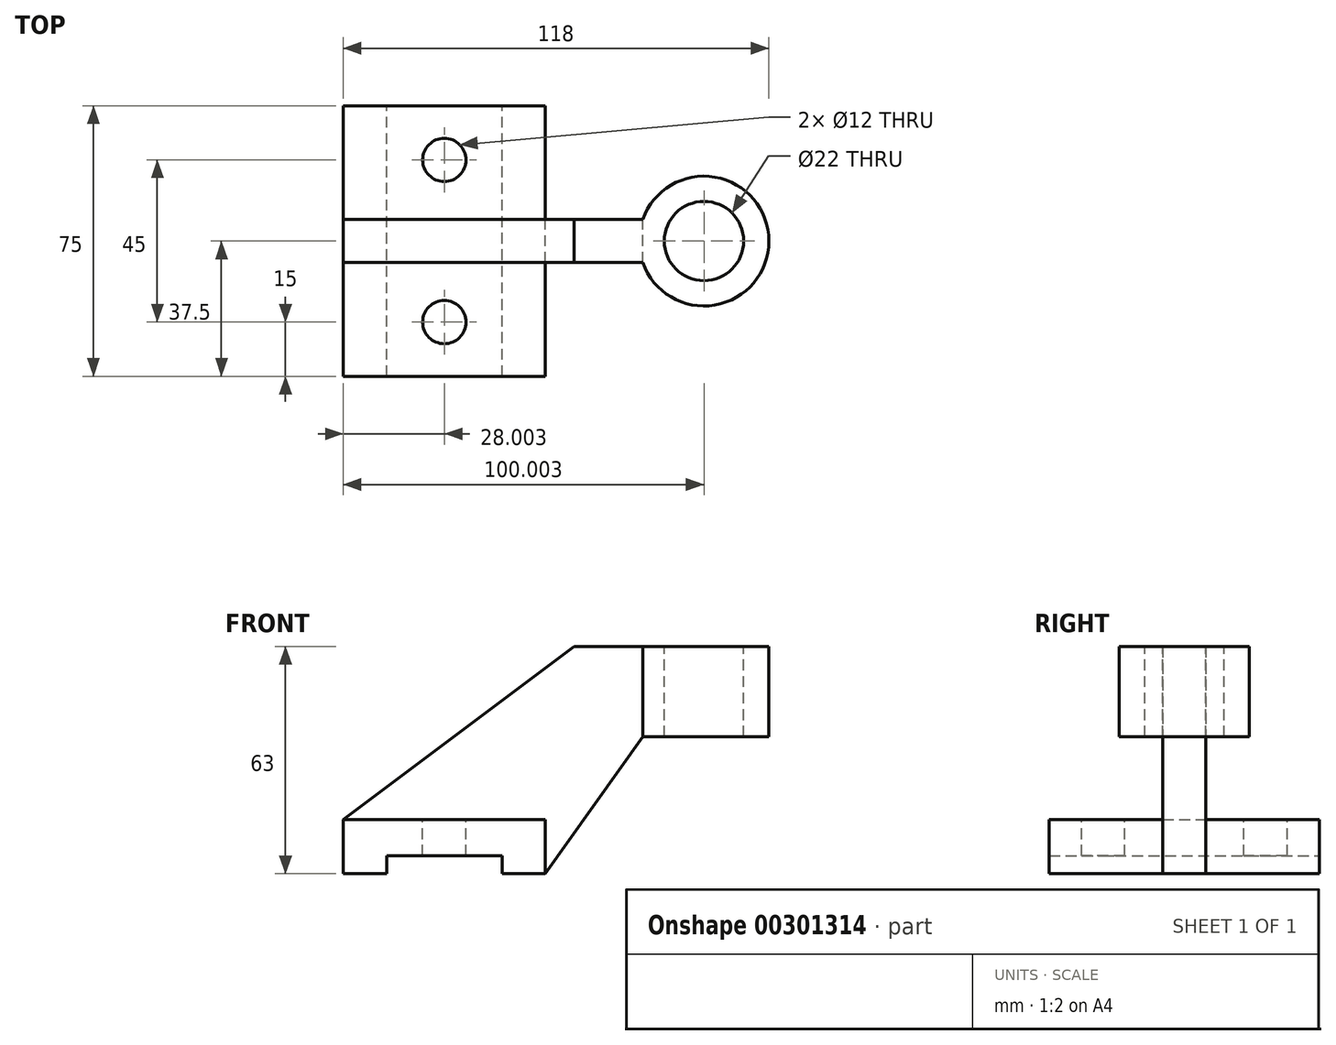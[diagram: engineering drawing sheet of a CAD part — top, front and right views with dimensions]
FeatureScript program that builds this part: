
annotation { "Feature Type Name" : "Feature", "Feature Type Description" : "" }
export const myFeature = defineFeature(function(context is Context, id is Id, definition is map)
    precondition{}
    {
        {
            var Q0;
            Q0=qCreatedBy(makeId("Top.planeOp"),FACE);
            var sketch = newSketch(context, id + "F0", { "sketchPlane" : qUnion([Q0])});
            skCircle(sketch, "E0", {"center": v(33.67, 0) * mm, "radius": 18 * mm});
            skCircle(sketch, "E1", {"center": v(33.67, 0) * mm, "radius": 11 * mm});
            skLineSegment(sketch, "E2", {"start": v(0, 0) * mm, "end": v(20, 0) * mm, "construction": true});
            skLineSegment(sketch, "E3", {"start": v(0, 0) * mm, "end": v(0, 6) * mm, "construction": true});
            skLineSegment(sketch, "E4", {"start": v(0, 6) * mm, "end": v(16.7, 6) * mm, "construction": true});
            skLineSegment(sketch, "E5", {"start": v(33.67, 0) * mm, "end": v(33.67, 22.5) * mm, "construction": true});
            skLineSegment(sketch, "E6", {"start": v(33.67, 22.5) * mm, "end": v(-38.33, 22.5) * mm, "construction": true});
            skLineSegment(sketch, "E7", {"start": v(-38.33, 22.5) * mm, "end": v(-38.33, -22.5) * mm, "construction": true});
            skCircle(sketch, "E8", {"center": v(-38.33, 22.5) * mm, "radius": 6 * mm});
            skCircle(sketch, "E9", {"center": v(-38.33, -22.5) * mm, "radius": 6 * mm});
            skLineSegment(sketch, "E10", {"start": v(16.7, 6) * mm, "end": v(16.7, 0) * mm, "construction": true});
            skPoint(sketch, "E11", {"position": v(16.7, 0) * mm});
            skSolve(sketch);
        }
        {
            var Q0;
            Q0=qCreatedBy(makeId("Front.planeOp"),FACE);
            var sketch = newSketch(context, id + "F1", { "sketchPlane" : qUnion([Q0])});
            skLineSegment(sketch, "E12", {"start": v(-66.33, -63) * mm, "end": v(-54.33, -63) * mm});
            skLineSegment(sketch, "E13", {"start": v(-54.33, -63) * mm, "end": v(-54.33, -58) * mm});
            skLineSegment(sketch, "E14", {"start": v(-54.33, -58) * mm, "end": v(-22.33, -58) * mm});
            skLineSegment(sketch, "E15", {"start": v(-22.33, -58) * mm, "end": v(-22.33, -63) * mm});
            skLineSegment(sketch, "E16", {"start": v(-22.33, -63) * mm, "end": v(-10.33, -63) * mm});
            skLineSegment(sketch, "E17", {"start": v(-10.33, -63) * mm, "end": v(-10.33, -48) * mm});
            skLineSegment(sketch, "E18", {"start": v(-10.33, -48) * mm, "end": v(-66.33, -48) * mm});
            skLineSegment(sketch, "E19", {"start": v(-66.33, -48) * mm, "end": v(-66.33, -63) * mm});
            skLineSegment(sketch, "E20", {"start": v(51.7, 0) * mm, "end": v(51.7, -25) * mm});
            skLineSegment(sketch, "E21", {"start": v(16.7, 0) * mm, "end": v(16.7, -25) * mm});
            skLineSegment(sketch, "E22", {"start": v(16.7, -25) * mm, "end": v(51.7, -25) * mm});
            skLineSegment(sketch, "E23", {"start": v(-10.33, -63) * mm, "end": v(16.7, -25) * mm});
            skLineSegment(sketch, "E24", {"start": v(-66.33, -48) * mm, "end": v(-2.33, 0) * mm});
            skLineSegment(sketch, "E25", {"start": v(-2.33, 0) * mm, "end": v(16.7, 0) * mm});
            skLineSegment(sketch, "E26", {"start": v(16.7, 0) * mm, "end": v(51.7, 0) * mm});
            skSolve(sketch);
        }
        {
            var Q0;
            Q0=makeQuery(id+"F1.imprint","IMPRINT",FACE,{"disambiguationData":[TD([[makeQuery(id+"F1.imprint","IMPRINT",EDGE,{"derivedFrom":sQuery(id+"F1.wireOp",EDGE,"E12")}),1.0]])]});
            extrude(context, id + "F2", {"entities" : qUnion([Q0]), "endBound" : BoundingType.SYMMETRIC, "depth" : 75 * mm});
        }
        {
            var Q0;
            Q0=makeQuery(id+"F1.imprint","IMPRINT",FACE,{"disambiguationData":[TD([[makeQuery(id+"F1.imprint","IMPRINT",EDGE,{"derivedFrom":sQuery(id+"F1.wireOp",EDGE,"E17")}),-1.0]])]});
            extrude(context, id + "F3", {"entities" : qUnion([Q0]), "operationType" : NewBodyOperationType.ADD, "endBound" : BoundingType.SYMMETRIC, "depth" : 12 * mm});
        }
        {
            var Q0;
            Q0=makeQuery(id+"F0.imprint","IMPRINT",FACE,{"disambiguationData":[TD([[makeQuery(id+"F0.imprint","IMPRINT",EDGE,{"derivedFrom":sQuery(id+"F0.wireOp",EDGE,"E0")}),1.0]])]});
            extrude(context, id + "F4", {"entities" : qUnion([Q0]), "operationType" : NewBodyOperationType.ADD, "oppositeDirection" : true, "depth" : 25 * mm});
        }
        {
            var Q0;
            Q0=makeQuery(id+"F0.imprint","IMPRINT",FACE,{"disambiguationData":[TD([[makeQuery(id+"F0.imprint","IMPRINT",EDGE,{"derivedFrom":sQuery(id+"F0.wireOp",EDGE,"E8")}),1.0]])]});
            var Q1;
            Q1=makeQuery(id+"F0.imprint","IMPRINT",FACE,{"disambiguationData":[TD([[makeQuery(id+"F0.imprint","IMPRINT",EDGE,{"derivedFrom":sQuery(id+"F0.wireOp",EDGE,"E9")}),1.0]])]});
            var Q2;
            Q2=sQuery(id+"F0.wireOp",EDGE,"E8");
            var Q3;
            Q3=sQuery(id+"F0.wireOp",EDGE,"E9");
            extrude(context, id + "F5", {"entities" : qUnion([Q0, Q1]), "operationType" : NewBodyOperationType.REMOVE, "surfaceEntities" : qUnion([Q2, Q3]), "endBound" : BoundingType.THROUGH_ALL, "oppositeDirection" : true, "depth" : 25 * mm});
        }
    });
